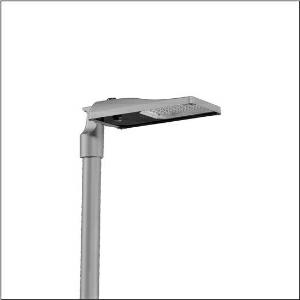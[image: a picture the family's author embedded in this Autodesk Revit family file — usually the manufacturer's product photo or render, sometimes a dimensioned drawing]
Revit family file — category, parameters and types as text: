
# Revit family: streetlight_sl_31_mini___st1_0a_5xh2d31t08ha_99ca
name_source: partatom
category: Lighting Fixtures
units: mm (PartAtom-declared; Revit-internal decimal feet)

## family parameters
Cut with Voids When Loaded = No
Host = Face
Light Source = No
Part Type = Normal
Room Calculation Point = No
Round Connector Dimension = Use Diameter
Shared = No

## types (1)
- --- (1 x LED, 9230 lm, 68.3 W, 3000K)
    Apparent Load = 68 VA
    CIE Flux Codes = 37 72 97 100 100
    Color Rendering = 70
    Color Temperature = 3000K
    Default Elevation = 1800 mm
    Description = Streetlight SL 31 mini D4i, Desk-Remote mast luminaire for post-top, side-entry; light control with lens of PMMA; light distribution: ST1.0a, direct asymmetric distribution, for standard-compliant lighting for roads and squares; LED: luminous flux: 9.230lm, light colour: 730, colour temperature: 3000K; luminous efficacy: 135,1lm/W; control: pre-setting: logarithmic dimming characteristic, flexible luminous flux parameterisation, time-dependent luminous flux control, constant luminous flux control, power reduction, intelligent temperature release in ECG and LED module, overheat protection; luminaire housing, of diecast aluminium, Siteco® metallic grey (DB 702S), corrosivity category C5 high according to DIN EN ISO 12944; cover of toughened safety glass, transparent, mast flange of diecast aluminium, Siteco® metallic grey (DB 702S), spigot size: 76/60mm, mast flange included unmounted; with cable H07RN-F 2x 1.5mm², cable length: 8,5m, connection cable pre-assembled; mains connection: 220..240V, AC, 50/60Hz; power consumption (at start of service life): 68,3W / (at end of service life): 74,5W / (with reduced operation 50%): 29,5W; protection rating (complete): IP66; insulation class (complete): insulation class II (safety insulation); impact resistance: IK09; certification: CE, ENEC, ENEC+, VDE, UKCA, ZD4i; permissible operating ambient temperature for outdoor applications: -40..+50°C; packaging unit: 1 piece

Light Distribution: ST1.0a
    Height = 76 mm
    Lamp = 1 x LED
    Lamp Light Flux = 9230 lm
    Lamp Power = 68.3 W
    Lamp count = 1
    Length = 547 mm
    Luminous efficacy = 135 lm/W
    Manufacturer = Siteco
    ModVariant = No
    Model = 5XH2D31T08HA
    Number of Poles = 1
    OnlyDefault = Yes
    Power Factor = 1
    Product Name = Streetlight SL 31 mini | ST1.0a
    Product group = mast luminaire | pylon top
    ProductGroupID = 6100
    Protection Class = Protection class II
    Protection Degree = IP 66
    RLX_Detail_Level = 1
    RLX_Emergency_Light_Flux = 0 lm
    RLX_Emergency_Type = 0
    RLX_Emergency_Type_DB = No
    RlxData = <blob elided: 39589 chars, md5=a2911889>
    Socket = socket
    Standby Power = 0 W
    System Light Flux = 9230 lm
    System Power = 68 W
    Type Comments = factory setting: luminous flux: 100 % | dim-lin: 254 | 692 mA
    Type Image = l_1300332.jpg
    URL = http://relux.com
    VarID = @adj_019493
    Voltage = 0 V
    Weight = 0.00 kg
    Width = 265 mm

## geometry (parser evidence)
native form markers: Blend x4, Sweep x9
no freeform markers — native parametric forms only
